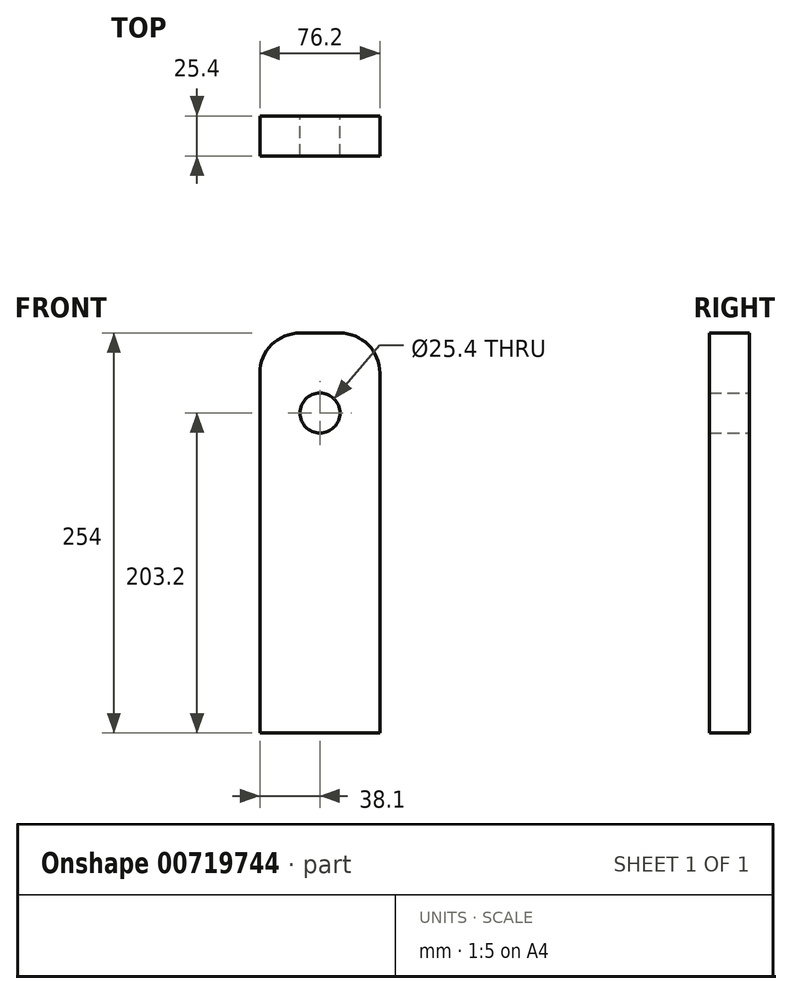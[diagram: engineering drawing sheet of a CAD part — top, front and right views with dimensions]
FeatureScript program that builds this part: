
annotation { "Feature Type Name" : "Feature", "Feature Type Description" : "" }
export const myFeature = defineFeature(function(context is Context, id is Id, definition is map)
    precondition{}
    {
        {
            var Q0;
            Q0=qCreatedBy(makeId("Front.planeOp"),FACE);
            var sketch = newSketch(context, id + "F0", { "sketchPlane" : qUnion([Q0])});
            skLineSegment(sketch, "E0.bottom", {"start": v(0, 0) * mm, "end": v(76.2, 0) * mm});
            skLineSegment(sketch, "E0.top", {"start": v(0, 254) * mm, "end": v(76.2, 254) * mm});
            skLineSegment(sketch, "E0.left", {"start": v(0, 0) * mm, "end": v(0, 254) * mm});
            skLineSegment(sketch, "E0.right", {"start": v(76.2, 0) * mm, "end": v(76.2, 254) * mm});
            skCircle(sketch, "E1", {"center": v(38.1, 203.2) * mm, "radius": 12.7 * mm});
            skSolve(sketch);
        }
        {
            var Q0;
            Q0 = qSketchRegion(id + "F0", true);
            extrude(context, id + "F1", {"entities" : qUnion([Q0]), "depth" : 25.4 * mm, "offsetDistance" : 25.4 * mm});
        }
        {
            var Q0;
            Q0=makeQuery(id+"F1.opExtrude","SWEPT_EDGE",EDGE,{"disambiguationData":[OSD([sQuery(id+"F0.wireOp",EDGE,"E0.top"),sQuery(id+"F0.wireOp",EDGE,"E0.left")])]});
            var Q1;
            Q1=makeQuery(id+"F1.opExtrude","SWEPT_EDGE",EDGE,{"disambiguationData":[OSD([sQuery(id+"F0.wireOp",EDGE,"E0.top"),sQuery(id+"F0.wireOp",EDGE,"E0.right")])]});
            fillet(context, id + "F2", {"entities" : qUnion([Q0, Q1]), "radius" : 25.4 * mm, "tangentPropagation" : true, "allowEdgeOverflow" : false});
        }
    });
